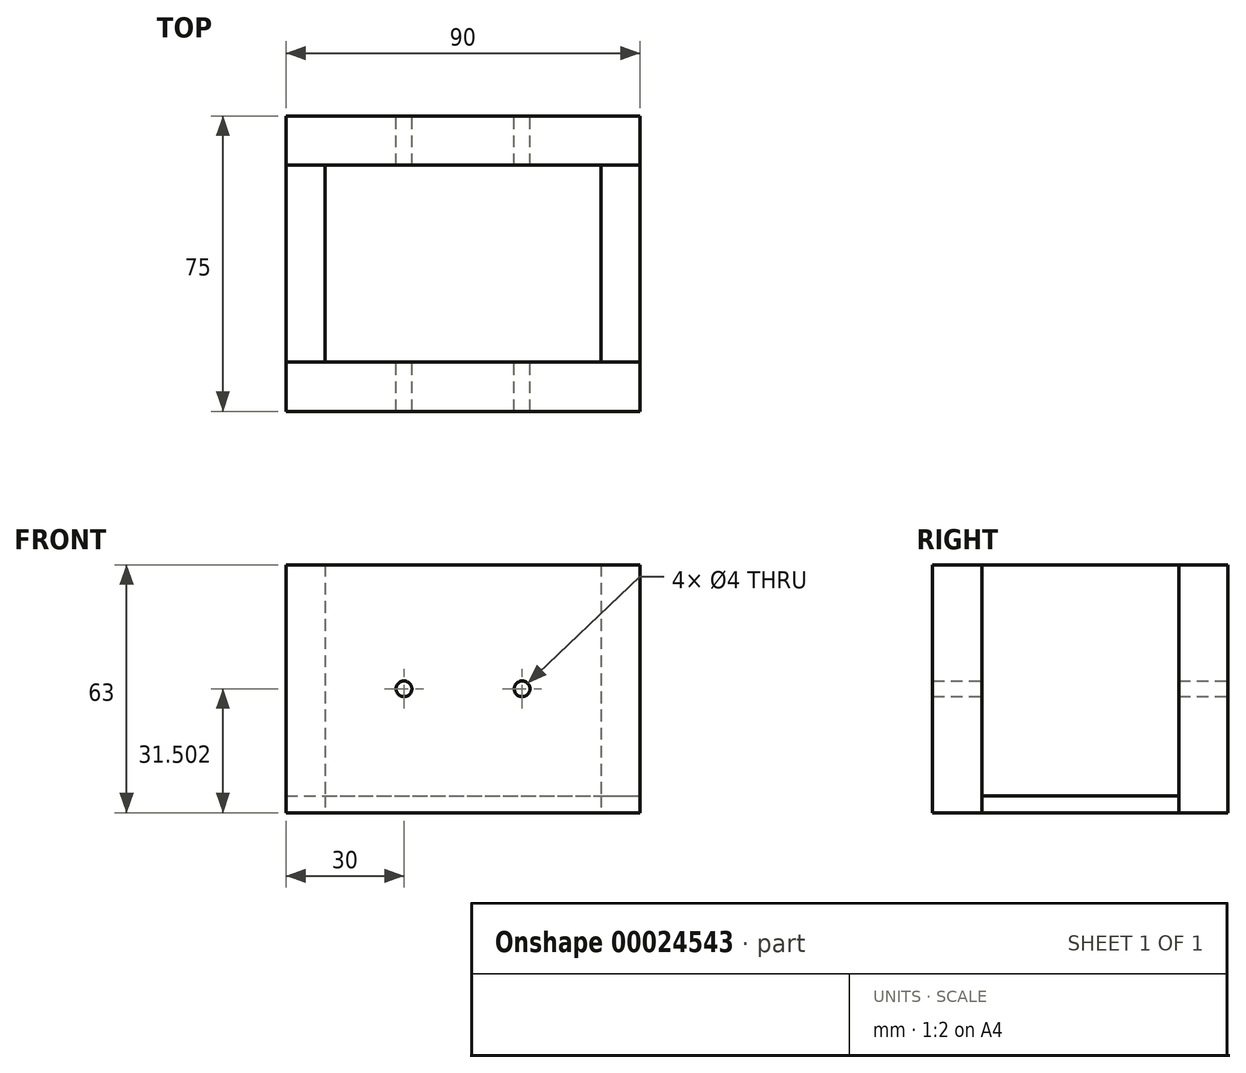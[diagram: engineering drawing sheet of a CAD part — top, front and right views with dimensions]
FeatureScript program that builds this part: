
annotation { "Feature Type Name" : "Feature", "Feature Type Description" : "" }
export const myFeature = defineFeature(function(context is Context, id is Id, definition is map)
    precondition{}
    {
        {
            var Q0;
            Q0=qCreatedBy(makeId("Front.planeOp"),FACE);
            var sketch = newSketch(context, id + "F0", { "sketchPlane" : qUnion([Q0])});
            skLineSegment(sketch, "E0.bottom", {"start": v(-60, 32.34) * mm, "end": v(30, 32.34) * mm});
            skLineSegment(sketch, "E0.top", {"start": v(-60, -30.66) * mm, "end": v(30, -30.66) * mm});
            skLineSegment(sketch, "E0.left", {"start": v(-60, 32.34) * mm, "end": v(-60, -30.66) * mm});
            skLineSegment(sketch, "E0.right", {"start": v(30, 32.34) * mm, "end": v(30, -30.66) * mm});
            skPoint(sketch, "E1", {"position": v(-30, -30.66) * mm});
            skPoint(sketch, "E2", {"position": v(0, -30.66) * mm});
            skCircle(sketch, "E3", {"center": v(-30, 0.84) * mm, "radius": 2 * mm});
            skCircle(sketch, "E4", {"center": v(0, 0.84) * mm, "radius": 2 * mm});
            skSolve(sketch);
        }
        {
            var Q0;
            Q0=makeQuery(id+"F0.imprint","IMPRINT",FACE,{"disambiguationData":[TD([[makeQuery(id+"F0.imprint","IMPRINT",EDGE,{"derivedFrom":sQuery(id+"F0.wireOp",EDGE,"E0.bottom")}),-1.0]])]});
            extrude(context, id + "F1", {"entities" : qUnion([Q0]), "depth" : 75 * mm});
        }
        {
            var Q0;
            Q0=makeQuery(id+"F1.opExtrude","SWEPT_FACE",FACE,{"disambiguationData":[OSD([sQuery(id+"F0.wireOp",EDGE,"E0.right")])]});
            var sketch = newSketch(context, id + "F2", { "sketchPlane" : qUnion([Q0])});
            skPoint(sketch, "E5", {"position": v(-50, 32.34) * mm});
            skPoint(sketch, "E6", {"position": v(-25, 32.34) * mm});
            skPoint(sketch, "E7", {"position": v(-75, 32.34) * mm});
            skPoint(sketch, "E8", {"position": v(0, 32.34) * mm});
            skLineSegment(sketch, "E9", {"start": v(-50, 32.34) * mm, "end": v(-50, -30.66) * mm});
            skLineSegment(sketch, "E10", {"start": v(-25, 32.34) * mm, "end": v(-25, -30.66) * mm});
            skPoint(sketch, "E11", {"position": v(-62.5, 32.34) * mm});
            skPoint(sketch, "E12", {"position": v(-12.5, 32.34) * mm});
            skLineSegment(sketch, "E13", {"start": v(-62.5, 32.34) * mm, "end": v(-62.5, -30.66) * mm});
            skLineSegment(sketch, "E14", {"start": v(-12.5, 32.34) * mm, "end": v(-12.5, -30.66) * mm});
            skSolve(sketch);
        }
        {
            var Q0;
            {var subQ3=sQuery(id+"F2.wireOp",EDGE,"E9");Q0=makeQuery(id+"F2.imprint","IMPRINT",FACE,{"disambiguationData":[TD([[makeQuery(id+"F2.imprint","IMPRINT",EDGE,{"derivedFrom":subQ3}),1.0]])]});}
            extrude(context, id + "F3", {"entities" : qUnion([Q0]), "operationType" : NewBodyOperationType.REMOVE, "oppositeDirection" : true, "depth" : 114.81 * mm});
        }
        {
            var Q0;
            {var subQ3=sQuery(id+"F2.wireOp",EDGE,"E9");Q0=makeQuery(id+"F2.imprint","IMPRINT",FACE,{"disambiguationData":[TD([[makeQuery(id+"F2.imprint","IMPRINT",EDGE,{"derivedFrom":subQ3}),-1.0]])]});}
            extrude(context, id + "F4", {"entities" : qUnion([Q0]), "operationType" : NewBodyOperationType.REMOVE, "oppositeDirection" : true, "depth" : 125.73 * mm});
        }
        {
            var Q0;
            {var subQ3=sQuery(id+"F2.wireOp",EDGE,"E10");Q0=makeQuery(id+"F2.imprint","IMPRINT",FACE,{"disambiguationData":[TD([[makeQuery(id+"F2.imprint","IMPRINT",EDGE,{"derivedFrom":subQ3}),1.0]])]});}
            extrude(context, id + "F5", {"entities" : qUnion([Q0]), "operationType" : NewBodyOperationType.REMOVE, "oppositeDirection" : true, "depth" : 142.55 * mm});
        }
        {
            var Q0;
            Q0=makeQuery(id+"F5.boolean.opBoolean","COPY",FACE,{"derivedFrom":makeQuery(id+"F5.opExtrude","SWEPT_FACE",FACE,{"disambiguationData":[OSD([sQuery(id+"F2.wireOp",EDGE,"E14")])]})});
            var sketch = newSketch(context, id + "F6", { "sketchPlane" : qUnion([Q0])});
            skPoint(sketch, "E15", {"position": v(20, 32.34) * mm});
            skPoint(sketch, "E16", {"position": v(-50, 32.34) * mm});
            skLineSegment(sketch, "E17", {"start": v(-50, 32.34) * mm, "end": v(-50, -30.66) * mm});
            skLineSegment(sketch, "E18", {"start": v(20, 32.34) * mm, "end": v(20, -30.66) * mm});
            skLineSegment(sketch, "E19", {"start": v(-60, -26.32) * mm, "end": v(30, -26.32) * mm});
            skSolve(sketch);
        }
        {
            var Q0;
            {var subQ6=sQuery(id+"F6.wireOp",EDGE,"E19");var subQ10=sQuery(id+"F6.wireOp",EDGE,"E17");var subQ12=makeQuery(id+"F6.imprint","INTERSECT",VERTEX,{"derivedFrom":[subQ10,subQ6]});Q0=makeQuery(id+"F6.imprint","IMPRINT",FACE,{"disambiguationData":[TD([[makeQuery(id+"F6.imprint","IMPRINT",EDGE,{"disambiguationData":[TD([[subQ12,1.0]])],"derivedFrom":subQ10}),-1.0]])]});}
            var Q1;
            Q1=makeQuery(id+"F4.boolean.opBoolean","COPY",FACE,{"derivedFrom":makeQuery(id+"F4.opExtrude","SWEPT_FACE",FACE,{"disambiguationData":[OSD([sQuery(id+"F2.wireOp",EDGE,"E13")])]})});
            extrude(context, id + "F7", {"entities" : qUnion([Q0]), "endBound" : BoundingType.UP_TO_SURFACE, "endBoundEntityFace" : qUnion([Q1]), "depth" : 49.4 * mm});
        }
        {
            var Q0;
            {var subQ0=sQuery(id+"F2.wireOp",EDGE,"E14");var subQ1=makeQuery(id+"F5.boolean.opBoolean","COPY",EDGE,{"derivedFrom":makeQuery(id+"F5.opExtrude","CAP_EDGE",EDGE,{"disambiguationData":[OSD([subQ0])],"isStart":true})});var subQ2=sQuery(id+"F6.wireOp",EDGE,"E19");var subQ3=makeQuery(id+"F6.imprint","INTERSECT",VERTEX,{"derivedFrom":[subQ1,subQ2]});Q0=makeQuery(id+"F6.imprint","IMPRINT",FACE,{"disambiguationData":[TD([[makeQuery(id+"F6.imprint","IMPRINT",EDGE,{"disambiguationData":[TD([[subQ3,1.0]])],"derivedFrom":subQ2}),1.0]])]});}
            var Q1;
            Q1=makeQuery(id+"F4.boolean.opBoolean","COPY",FACE,{"derivedFrom":makeQuery(id+"F4.opExtrude","SWEPT_FACE",FACE,{"disambiguationData":[OSD([sQuery(id+"F2.wireOp",EDGE,"E13")])]})});
            extrude(context, id + "F8", {"entities" : qUnion([Q0]), "endBound" : BoundingType.UP_TO_SURFACE, "endBoundEntityFace" : qUnion([Q1]), "depth" : 25 * mm});
        }
        {
            var Q0;
            {var subQ0=sQuery(id+"F2.wireOp",EDGE,"E14");var subQ1=makeQuery(id+"F5.boolean.opBoolean","COPY",EDGE,{"derivedFrom":makeQuery(id+"F5.opExtrude","CAP_EDGE",EDGE,{"disambiguationData":[OSD([subQ0])],"isStart":true})});var subQ2=sQuery(id+"F6.wireOp",EDGE,"E19");var subQ3=makeQuery(id+"F6.imprint","INTERSECT",VERTEX,{"derivedFrom":[subQ1,subQ2]});Q0=makeQuery(id+"F6.imprint","IMPRINT",FACE,{"disambiguationData":[TD([[makeQuery(id+"F6.imprint","IMPRINT",EDGE,{"disambiguationData":[TD([[subQ3,1.0]])],"derivedFrom":subQ2}),-1.0]])]});}
            var Q1;
            Q1=makeQuery(id+"F4.boolean.opBoolean","COPY",FACE,{"derivedFrom":makeQuery(id+"F4.opExtrude","SWEPT_FACE",FACE,{"disambiguationData":[OSD([sQuery(id+"F2.wireOp",EDGE,"E13")])]})});
            extrude(context, id + "F9", {"entities" : qUnion([Q0]), "endBound" : BoundingType.UP_TO_SURFACE, "endBoundEntityFace" : qUnion([Q1]), "depth" : 46.22 * mm});
        }
        {
            var Q0;
            {var subQ6=sQuery(id+"F6.wireOp",EDGE,"E19");var subQ10=sQuery(id+"F6.wireOp",EDGE,"E17");var subQ12=makeQuery(id+"F6.imprint","INTERSECT",VERTEX,{"derivedFrom":[subQ10,subQ6]});Q0=makeQuery(id+"F6.imprint","IMPRINT",FACE,{"disambiguationData":[TD([[makeQuery(id+"F6.imprint","IMPRINT",EDGE,{"disambiguationData":[TD([[subQ12,-1.0]])],"derivedFrom":subQ10}),-1.0]])]});}
            var Q1;
            Q1=makeQuery(id+"F4.boolean.opBoolean","COPY",FACE,{"derivedFrom":makeQuery(id+"F4.opExtrude","SWEPT_FACE",FACE,{"disambiguationData":[OSD([sQuery(id+"F2.wireOp",EDGE,"E13")])]})});
            extrude(context, id + "F10", {"entities" : qUnion([Q0]), "endBound" : BoundingType.UP_TO_SURFACE, "endBoundEntityFace" : qUnion([Q1]), "depth" : 25 * mm});
        }
        {
            var Q0;
            {var subQ3=sQuery(id+"F6.wireOp",EDGE,"E17");var subQ5=sQuery(id+"F6.wireOp",EDGE,"E19");var subQ7=makeQuery(id+"F6.imprint","INTERSECT",VERTEX,{"derivedFrom":[subQ3,subQ5]});Q0=makeQuery(id+"F6.imprint","IMPRINT",FACE,{"disambiguationData":[TD([[makeQuery(id+"F6.imprint","IMPRINT",EDGE,{"disambiguationData":[TD([[subQ7,-1.0]])],"derivedFrom":subQ5}),-1.0]])]});}
            var Q1;
            Q1=makeQuery(id+"F4.boolean.opBoolean","COPY",FACE,{"derivedFrom":makeQuery(id+"F4.opExtrude","SWEPT_FACE",FACE,{"disambiguationData":[OSD([sQuery(id+"F2.wireOp",EDGE,"E13")])]})});
            extrude(context, id + "F11", {"entities" : qUnion([Q0]), "endBound" : BoundingType.UP_TO_SURFACE, "endBoundEntityFace" : qUnion([Q1]), "depth" : 25 * mm});
        }
    });
